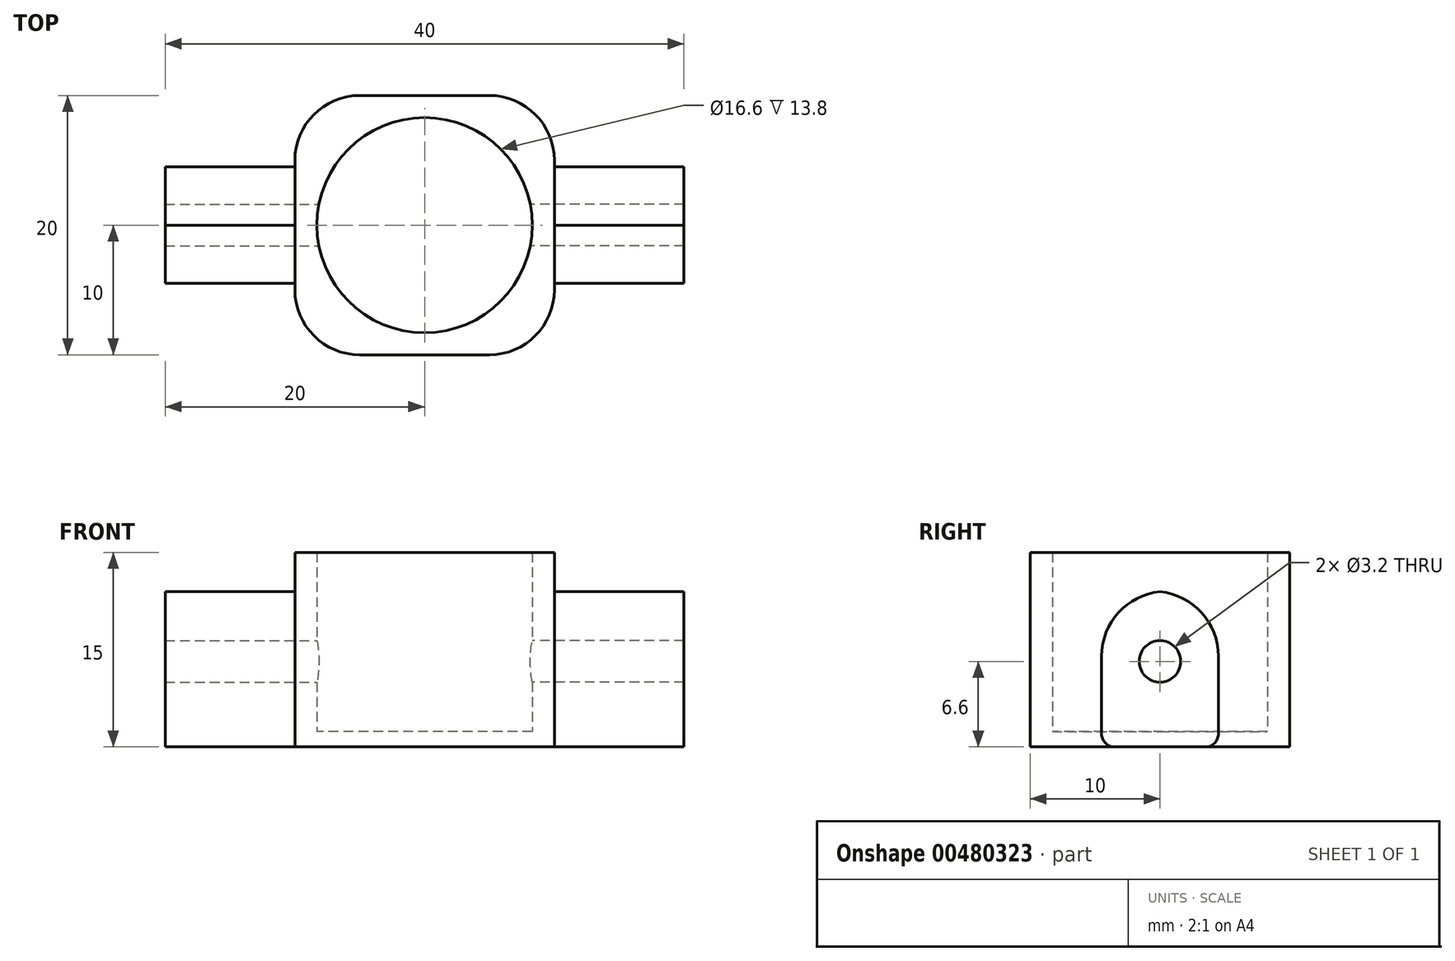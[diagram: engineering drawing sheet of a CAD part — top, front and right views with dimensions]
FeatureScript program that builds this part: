
annotation { "Feature Type Name" : "Feature", "Feature Type Description" : "" }
export const myFeature = defineFeature(function(context is Context, id is Id, definition is map)
    precondition{}
    {
        {
            var Q0;
            Q0=qCreatedBy(makeId("Top.planeOp"),FACE);
            var sketch = newSketch(context, id + "F0", { "sketchPlane" : qUnion([Q0])});
            skLineSegment(sketch, "E0.bottom", {"start": v(-10, 10) * mm, "end": v(10, 10) * mm});
            skLineSegment(sketch, "E0.top", {"start": v(-10, -10) * mm, "end": v(10, -10) * mm});
            skLineSegment(sketch, "E0.left", {"start": v(-10, 10) * mm, "end": v(-10, -10) * mm});
            skLineSegment(sketch, "E0.right", {"start": v(10, 10) * mm, "end": v(10, -10) * mm});
            skPoint(sketch, "E0.middle", {"position": v(0, 0) * mm});
            skCircle(sketch, "E1", {"center": v(0, 0) * mm, "radius": 8.3 * mm});
            skSolve(sketch);
        }
        {
            var Q0;
            Q0=makeQuery(id+"F0.imprint","IMPRINT",FACE,{"disambiguationData":[TD([[makeQuery(id+"F0.imprint","IMPRINT",EDGE,{"derivedFrom":sQuery(id+"F0.wireOp",EDGE,"E0.bottom")}),-1.0]])]});
            extrude(context, id + "F1", {"entities" : qUnion([Q0]), "depth" : 15 * mm});
        }
        {
            var Q0;
            Q0=makeQuery(id+"F1.opExtrude","SWEPT_FACE",FACE,{"disambiguationData":[OSD([sQuery(id+"F0.wireOp",EDGE,"E0.left")])]});
            var sketch = newSketch(context, id + "F2", { "sketchPlane" : qUnion([Q0])});
            skLineSegment(sketch, "E2.0", {"start": v(-10, 15) * mm, "end": v(-10, 0) * mm});
            skLineSegment(sketch, "E3.0", {"start": v(-10, 0) * mm, "end": v(10, 0) * mm});
            skLineSegment(sketch, "E4.0", {"start": v(10, 15) * mm, "end": v(10, 0) * mm});
            skLineSegment(sketch, "E5", {"start": v(-4.5, 0) * mm, "end": v(-4.5, 12) * mm});
            skLineSegment(sketch, "E6", {"start": v(-4.5, 12) * mm, "end": v(4.5, 12) * mm});
            skLineSegment(sketch, "E7", {"start": v(4.5, 12) * mm, "end": v(4.5, 0) * mm});
            skSolve(sketch);
        }
        {
            var Q0;
            {var subQ0=sQuery(id+"F2.wireOp",EDGE,"E5");Q0=makeQuery(id+"F2.imprint","IMPRINT",FACE,{"disambiguationData":[TD([[makeQuery(id+"F2.imprint","IMPRINT",EDGE,{"derivedFrom":subQ0}),-1.0]])]});}
            extrude(context, id + "F3", {"entities" : qUnion([Q0]), "operationType" : NewBodyOperationType.ADD, "depth" : 10 * mm});
        }
        {
            var Q0;
            Q0=makeQuery(id+"F1.opExtrude","SWEPT_FACE",FACE,{"disambiguationData":[OSD([sQuery(id+"F0.wireOp",EDGE,"E0.right")])]});
            var sketch = newSketch(context, id + "F4", { "sketchPlane" : qUnion([Q0])});
            skLineSegment(sketch, "E8.0", {"start": v(10, 0) * mm, "end": v(-10, 0) * mm});
            skLineSegment(sketch, "E9.0", {"start": v(10, 15) * mm, "end": v(10, 0) * mm});
            skLineSegment(sketch, "E10.0", {"start": v(-10, 15) * mm, "end": v(-10, 0) * mm});
            skLineSegment(sketch, "E11", {"start": v(-4.5, 0) * mm, "end": v(-4.5, 12) * mm});
            skLineSegment(sketch, "E12", {"start": v(-4.5, 12) * mm, "end": v(4.5, 12) * mm});
            skLineSegment(sketch, "E13", {"start": v(4.5, 12) * mm, "end": v(4.5, 0) * mm});
            skCircle(sketch, "E14", {"center": v(0, 6.6) * mm, "radius": 1.6 * mm});
            skSolve(sketch);
        }
        {
            var Q0;
            {var subQ1=sQuery(id+"F4.wireOp",EDGE,"E11");Q0=makeQuery(id+"F4.imprint","IMPRINT",FACE,{"disambiguationData":[TD([[makeQuery(id+"F4.imprint","IMPRINT",EDGE,{"derivedFrom":subQ1}),-1.0]])]});}
            extrude(context, id + "F5", {"entities" : qUnion([Q0]), "operationType" : NewBodyOperationType.ADD, "depth" : 10 * mm});
        }
        {
            var Q0;
            Q0=makeQuery(id+"F4.imprint","IMPRINT",FACE,{"disambiguationData":[TD([[makeQuery(id+"F4.imprint","IMPRINT",EDGE,{"derivedFrom":sQuery(id+"F4.wireOp",EDGE,"E14")}),1.0]])]});
            extrude(context, id + "F6", {"entities" : qUnion([Q0]), "operationType" : NewBodyOperationType.REMOVE, "endBound" : BoundingType.THROUGH_ALL, "oppositeDirection" : true, "depth" : 25 * mm});
        }
        {
            var Q0;
            Q0=makeQuery(id+"F0.imprint","IMPRINT",FACE,{"disambiguationData":[TD([[makeQuery(id+"F0.imprint","IMPRINT",EDGE,{"derivedFrom":sQuery(id+"F0.wireOp",EDGE,"E1")}),1.0]])]});
            extrude(context, id + "F7", {"entities" : qUnion([Q0]), "operationType" : NewBodyOperationType.ADD, "depth" : 1.2 * mm});
        }
        {
            var Q0;
            Q0=makeQuery(id+"F1.opExtrude","SWEPT_EDGE",EDGE,{"disambiguationData":[OSD([sQuery(id+"F0.wireOp",EDGE,"E0.top"),sQuery(id+"F0.wireOp",EDGE,"E0.left")])]});
            var Q1;
            Q1=makeQuery(id+"F1.opExtrude","SWEPT_EDGE",EDGE,{"disambiguationData":[OSD([sQuery(id+"F0.wireOp",EDGE,"E0.top"),sQuery(id+"F0.wireOp",EDGE,"E0.right")])]});
            var Q2;
            Q2=makeQuery(id+"F3.opExtrude","SWEPT_EDGE",EDGE,{"disambiguationData":[OSD([sQuery(id+"F2.wireOp",EDGE,"E5"),sQuery(id+"F2.wireOp",EDGE,"E6")])]});
            var Q3;
            Q3=makeQuery(id+"F3.opExtrude","SWEPT_EDGE",EDGE,{"disambiguationData":[OSD([sQuery(id+"F2.wireOp",EDGE,"E6"),sQuery(id+"F2.wireOp",EDGE,"E7")])]});
            var Q4;
            Q4=makeQuery(id+"F1.opExtrude","SWEPT_EDGE",EDGE,{"disambiguationData":[OSD([sQuery(id+"F0.wireOp",EDGE,"E0.bottom"),sQuery(id+"F0.wireOp",EDGE,"E0.left")])]});
            var Q5;
            Q5=makeQuery(id+"F1.opExtrude","SWEPT_EDGE",EDGE,{"disambiguationData":[OSD([sQuery(id+"F0.wireOp",EDGE,"E0.bottom"),sQuery(id+"F0.wireOp",EDGE,"E0.right")])]});
            var Q6;
            Q6=makeQuery(id+"F5.opExtrude","SWEPT_EDGE",EDGE,{"disambiguationData":[OSD([sQuery(id+"F4.wireOp",EDGE,"E12"),sQuery(id+"F4.wireOp",EDGE,"E13")])]});
            var Q7;
            Q7=makeQuery(id+"F5.opExtrude","SWEPT_EDGE",EDGE,{"disambiguationData":[OSD([sQuery(id+"F4.wireOp",EDGE,"E11"),sQuery(id+"F4.wireOp",EDGE,"E12")])]});
            fillet(context, id + "F8", {"entities" : qUnion([Q0, Q1, Q2, Q3, Q4, Q5, Q6, Q7]), "radius" : 5 * mm, "tangentPropagation" : true, "allowEdgeOverflow" : false});
        }
        {
            var Q0;
            Q0=makeQuery(id+"F5.opExtrude","SWEPT_EDGE",EDGE,{"disambiguationData":[OSD([sQuery(id+"F4.wireOp",EDGE,"E8.0"),sQuery(id+"F4.wireOp",EDGE,"E11")])]});
            var Q1;
            Q1=makeQuery(id+"F5.opExtrude","SWEPT_EDGE",EDGE,{"disambiguationData":[OSD([sQuery(id+"F4.wireOp",EDGE,"E8.0"),sQuery(id+"F4.wireOp",EDGE,"E13")])]});
            var Q2;
            Q2=makeQuery(id+"F3.opExtrude","SWEPT_EDGE",EDGE,{"disambiguationData":[OSD([sQuery(id+"F2.wireOp",EDGE,"E3.0"),sQuery(id+"F2.wireOp",EDGE,"E5")])]});
            var Q3;
            Q3=makeQuery(id+"F3.opExtrude","SWEPT_EDGE",EDGE,{"disambiguationData":[OSD([sQuery(id+"F2.wireOp",EDGE,"E3.0"),sQuery(id+"F2.wireOp",EDGE,"E7")])]});
            fillet(context, id + "F9", {"entities" : qUnion([Q0, Q1, Q2, Q3]), "radius" : 1 * mm, "tangentPropagation" : true, "allowEdgeOverflow" : false});
        }
    });
